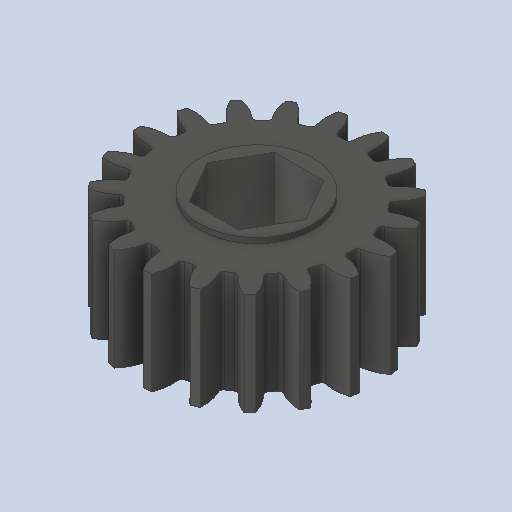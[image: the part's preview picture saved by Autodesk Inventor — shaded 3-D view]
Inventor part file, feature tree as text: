
AUTODESK INVENTOR PART (.ipt)
format: ipt  version: 2023.4 (Build 274418000, 418)  size: 238,080 bytes
history: native  units: in
note: dims shown in document units (in); Inventor stores cm internally (conversion verified against a paired STEP export)
features: fillet x1
ambient origin geometry x8: Origin, YZ Plane, XZ Plane, XY Plane, X Axis, Y Axis, Z Axis, Center Point
bodies: Solid1 (feature_tree)
feature tree (1):
  fillet  "Fillet1"  [1 undecoded]
note: 1 required parameter value undecoded (feature->parameter linkage not recoverable at this tier; creation-order binding heuristic only, values carry confidence <= 0.55)
